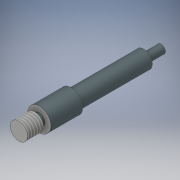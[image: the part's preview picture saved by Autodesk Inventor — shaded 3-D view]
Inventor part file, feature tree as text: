
AUTODESK INVENTOR PART (.ipt)
format: ipt  version: 2017 (Build 210142000, 142)  size: 124,928 bytes
history: native  units: mm
features: extrude x5, sketch x5, thread x1
ambient origin geometry x8: Origin, YZ Plane, XZ Plane, XY Plane, X Axis, Y Axis, Z Axis, Center Point
bodies: Solid1 (feature_tree)
feature tree (11):
  extrude  "Extrusion1"  Depth=5.5mm TaperAngle=0.0deg
  extrude  "Extrusion2"  Depth=1.5mm TaperAngle=0.0deg
  extrude  "Extrusion3"  Depth=11.0mm TaperAngle=0.0deg
  extrude  "Extrusion4"  Depth=25.0mm TaperAngle=0.0deg
  extrude  "Extrusion5"  Depth=6.0mm TaperAngle=0.0deg
  thread  "Thread1"  [1 undecoded]
  sketch  "Sketch1"  dims[d0=6.0mm d1=5.5mm d2=0.0mm]
  sketch  "Sketch2"  dims[d3=4.0mm d4=1.5mm d5=0.0mm]
  sketch  "Sketch3"  dims[d6=8.0mm d7=11.0mm d8=0.0mm]
  sketch  "Sketch4"  dims[d9=6.0mm d10=25.0mm d11=0.0mm]
  sketch  "Sketch5"  dims[d12=3.0mm d13=6.0mm d14=0.0mm d15=10.0mm d16=0.0mm]
note: 1 required parameter value undecoded (feature->parameter linkage not recoverable at this tier; creation-order binding heuristic only, values carry confidence <= 0.55)
